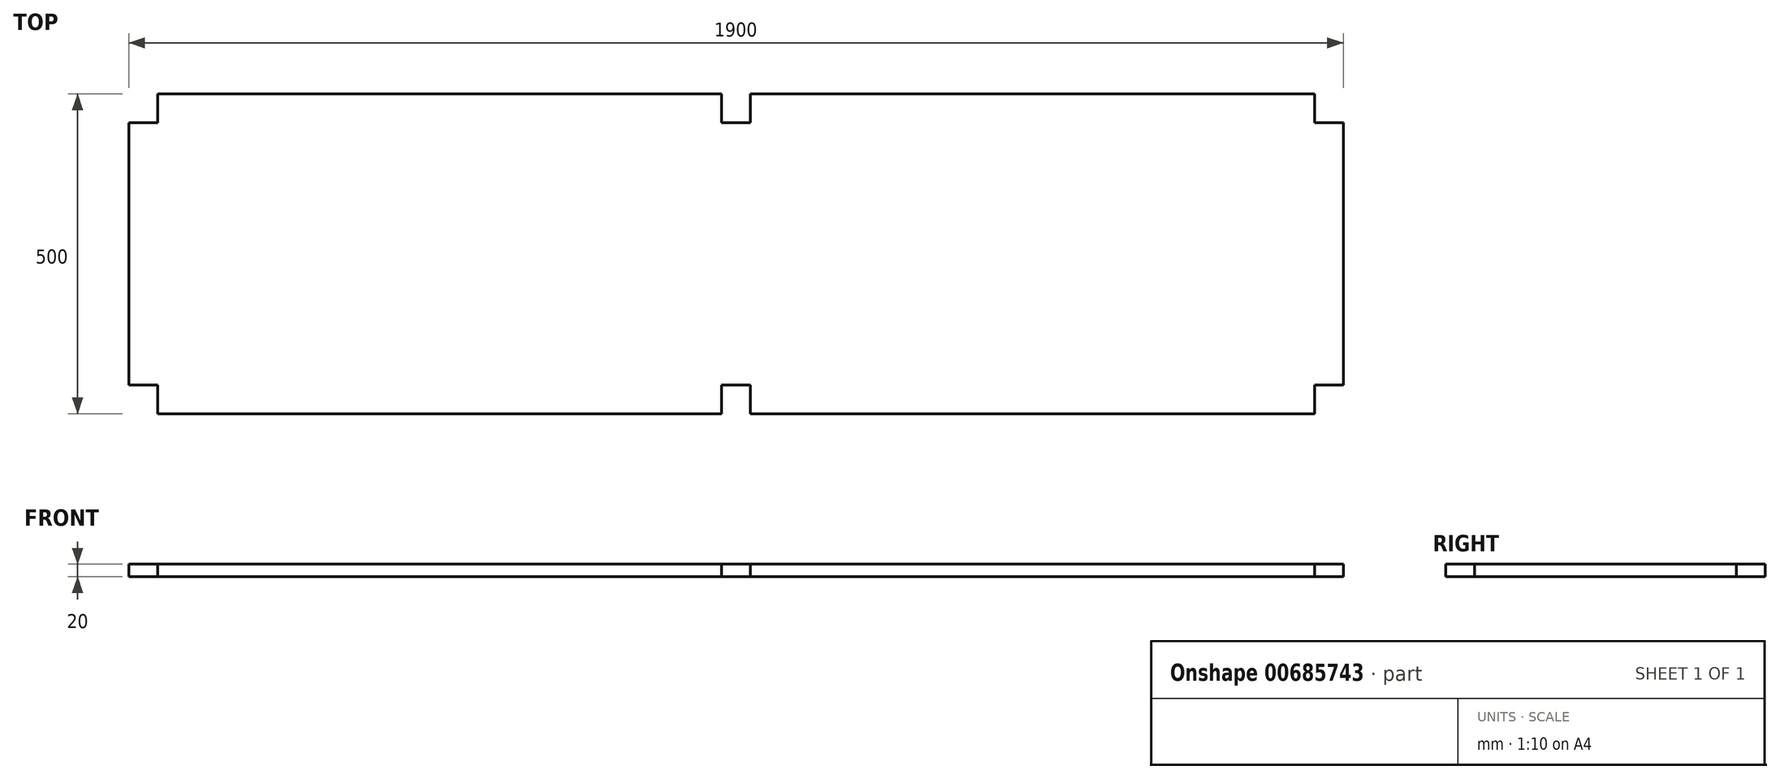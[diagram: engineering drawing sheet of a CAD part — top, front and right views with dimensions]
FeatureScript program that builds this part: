
annotation { "Feature Type Name" : "Feature", "Feature Type Description" : "" }
export const myFeature = defineFeature(function(context is Context, id is Id, definition is map)
    precondition{}
    {
        {
            var Q0;
            Q0=qCreatedBy(makeId("Top.planeOp"),FACE);
            var sketch = newSketch(context, id + "F0", { "sketchPlane" : qUnion([Q0])});
            skLineSegment(sketch, "E0.bottom", {"start": v(950, 250) * mm, "end": v(-950, 250) * mm});
            skLineSegment(sketch, "E0.top", {"start": v(950, -250) * mm, "end": v(-950, -250) * mm});
            skLineSegment(sketch, "E0.left", {"start": v(950, 250) * mm, "end": v(950, -250) * mm});
            skLineSegment(sketch, "E0.right", {"start": v(-950, 250) * mm, "end": v(-950, -250) * mm});
            skPoint(sketch, "E0.middle", {"position": v(0, 0) * mm});
            skSolve(sketch);
        }
        {
            var Q0;
            Q0=qSketchRegion(id+"F0",true);
            extrude(context, id + "F1", {"entities" : qUnion([Q0]), "depth" : 20 * mm, "offsetDistance" : 25 * mm});
        }
        {
            var Q0;
            Q0=makeQuery(id+"F1.opExtrude","CAP_FACE",FACE,{"disambiguationData":[OSD([sQuery(id+"F0.wireOp",EDGE,"E0.bottom"),sQuery(id+"F0.wireOp",EDGE,"E0.top"),sQuery(id+"F0.wireOp",EDGE,"E0.left"),sQuery(id+"F0.wireOp",EDGE,"E0.right")])],"isStart":false});
            var sketch = newSketch(context, id + "F2", { "sketchPlane" : qUnion([Q0])});
            skLineSegment(sketch, "E1.bottom", {"start": v(-950, 250) * mm, "end": v(-905, 250) * mm});
            skLineSegment(sketch, "E1.top", {"start": v(-950, 205) * mm, "end": v(-905, 205) * mm});
            skLineSegment(sketch, "E1.left", {"start": v(-950, 250) * mm, "end": v(-950, 205) * mm});
            skLineSegment(sketch, "E1.right", {"start": v(-905, 250) * mm, "end": v(-905, 205) * mm});
            skLineSegment(sketch, "E2.bottom", {"start": v(-950, -250) * mm, "end": v(-905, -250) * mm});
            skLineSegment(sketch, "E2.top", {"start": v(-950, -205) * mm, "end": v(-905, -205) * mm});
            skLineSegment(sketch, "E2.left", {"start": v(-950, -250) * mm, "end": v(-950, -205) * mm});
            skLineSegment(sketch, "E2.right", {"start": v(-905, -250) * mm, "end": v(-905, -205) * mm});
            skLineSegment(sketch, "E3.bottom", {"start": v(950, 250) * mm, "end": v(905, 250) * mm});
            skLineSegment(sketch, "E3.top", {"start": v(950, 205) * mm, "end": v(905, 205) * mm});
            skLineSegment(sketch, "E3.left", {"start": v(950, 250) * mm, "end": v(950, 205) * mm});
            skLineSegment(sketch, "E3.right", {"start": v(905, 250) * mm, "end": v(905, 205) * mm});
            skLineSegment(sketch, "E4.bottom", {"start": v(950, -250) * mm, "end": v(905, -250) * mm});
            skLineSegment(sketch, "E4.top", {"start": v(950, -205) * mm, "end": v(905, -205) * mm});
            skLineSegment(sketch, "E4.left", {"start": v(950, -250) * mm, "end": v(950, -205) * mm});
            skLineSegment(sketch, "E4.right", {"start": v(905, -250) * mm, "end": v(905, -205) * mm});
            skLineSegment(sketch, "E5.bottom", {"start": v(22.5, 250) * mm, "end": v(-22.5, 250) * mm});
            skLineSegment(sketch, "E5.top", {"start": v(22.5, 205) * mm, "end": v(-22.5, 205) * mm});
            skLineSegment(sketch, "E5.left", {"start": v(22.5, 250) * mm, "end": v(22.5, 205) * mm});
            skLineSegment(sketch, "E5.right", {"start": v(-22.5, 250) * mm, "end": v(-22.5, 205) * mm});
            skPoint(sketch, "E5.middle", {"position": v(0, 227.5) * mm});
            skPoint(sketch, "E5.middle.positionSnap0", {"position": v(0, 250) * mm});
            skPoint(sketch, "E5.centerSnap0", {"position": v(0, 250) * mm});
            skLineSegment(sketch, "E6.bottom", {"start": v(22.5, -250) * mm, "end": v(-22.5, -250) * mm});
            skLineSegment(sketch, "E6.top", {"start": v(22.5, -205) * mm, "end": v(-22.5, -205) * mm});
            skLineSegment(sketch, "E6.left", {"start": v(22.5, -250) * mm, "end": v(22.5, -205) * mm});
            skLineSegment(sketch, "E6.right", {"start": v(-22.5, -250) * mm, "end": v(-22.5, -205) * mm});
            skPoint(sketch, "E6.middle", {"position": v(0, -227.5) * mm});
            skSolve(sketch);
        }
        {
            var Q0;
            Q0=qSketchRegion(id+"F2",true);
            extrude(context, id + "F3", {"entities" : qUnion([Q0]), "operationType" : NewBodyOperationType.REMOVE, "endBound" : BoundingType.THROUGH_ALL, "oppositeDirection" : true, "depth" : 25 * mm, "offsetDistance" : 25 * mm});
        }
    });
